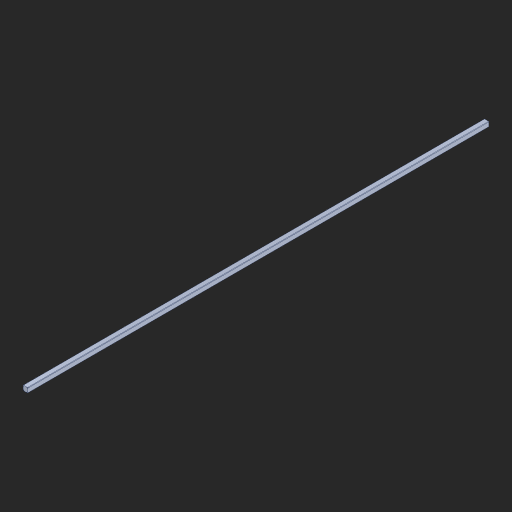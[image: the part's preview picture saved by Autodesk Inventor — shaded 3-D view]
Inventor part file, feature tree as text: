
AUTODESK INVENTOR PART (.ipt)
format: ipt  version: 2023 (Build 270158000, 158)  size: 168,960 bytes
history: native  units: in
note: dims shown in document units (in); Inventor stores cm internally (conversion verified against a paired STEP export)
features: other x26, thicken_offset x1, extrude x1, sketch x1
ambient origin geometry x8: Origin, YZ Plane, XZ Plane, XY Plane, X Axis, Y Axis, Z Axis, Center Point
bodies: Solid1 (feature_tree)
feature tree (29):
  other  "Table"
  other  "Shaft LS 0.5"
  other  "Shaft LS 1.0"
  other  "Shaft LS 1.5"
  other  "Shaft LS 2.0"
  other  "Shaft LS 2.5"
  other  "Shaft LS 3.0"
  other  "Shaft LS 3.5"
  other  "Shaft LS 4.0"
  other  "Shaft LS 4.5"
  other  "Shaft LS 5.0"
  other  "Shaft LS 5.5"
  other  "Shaft LS 6.0"
  other  "Shaft LS 6.5"
  other  "Shaft LS 7.0"
  other  "Shaft LS 7.5"
  other  "Shaft LS 8.0"
  other  "Shaft LS 8.5"
  other  "Shaft LS 9.0"
  other  "Shaft LS 9.5"
  other  "Shaft LS 10.0"
  other  "Shaft LS 10.5"
  other  "Shaft LS 11.0"
  other  "Shaft LS 11.5"
  other  "Shaft LS 12.0"
  thicken_offset  "Thicken1"
  extrude  "Extrusion1"  Depth=0.125in
  sketch  "Sketch1"  dims[d0=0.125in d1=0.125in d2=0.125in d3=0.0in]
  parser-record x1  (decoder bookkeeping rows leaked as tree rows — omitted from the tree; the rows remain in map.json)
